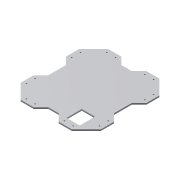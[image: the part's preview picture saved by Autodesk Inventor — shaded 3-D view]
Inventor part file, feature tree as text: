
AUTODESK INVENTOR PART (.ipt)
format: ipt  version: 2014 (Build 180170000, 170)  size: 156,160 bytes
history: native  units: mm
features: extrude x3, sketch x3, mirror x1
ambient origin geometry x8: Origin, YZ Plane, XZ Plane, XY Plane, X Axis, Y Axis, Z Axis, Center Point
bodies: Solid1 (feature_tree)
feature tree (7):
  extrude  "Extrusion1"  Depth=225.0mm
  extrude  "Extrusion2"  Depth=25.0mm
  mirror  "Mirror1"
  extrude  "Extrusion3"  Depth=45.0mm
  sketch  "Sketch1"  dims[d0=250.0mm d1=225.0mm]
  sketch  "Sketch2"  dims[d2=5.0mm d3=0.0mm d4=25.0mm]
  sketch  "Sketch3"  dims[d5=25.0mm d6=45.0mm d7=12.5mm d8=12.5mm d9=4.5mm d10=30.0mm d11=30.0mm d12=30.0mm d13=7.5mm d14=7.5mm d15=7.5mm d16=12.5mm d17=5.0mm d18=0.0mm d19=45.0mm d20=52.0mm d21=45.0mm d22=5.0mm d23=0.0mm]
